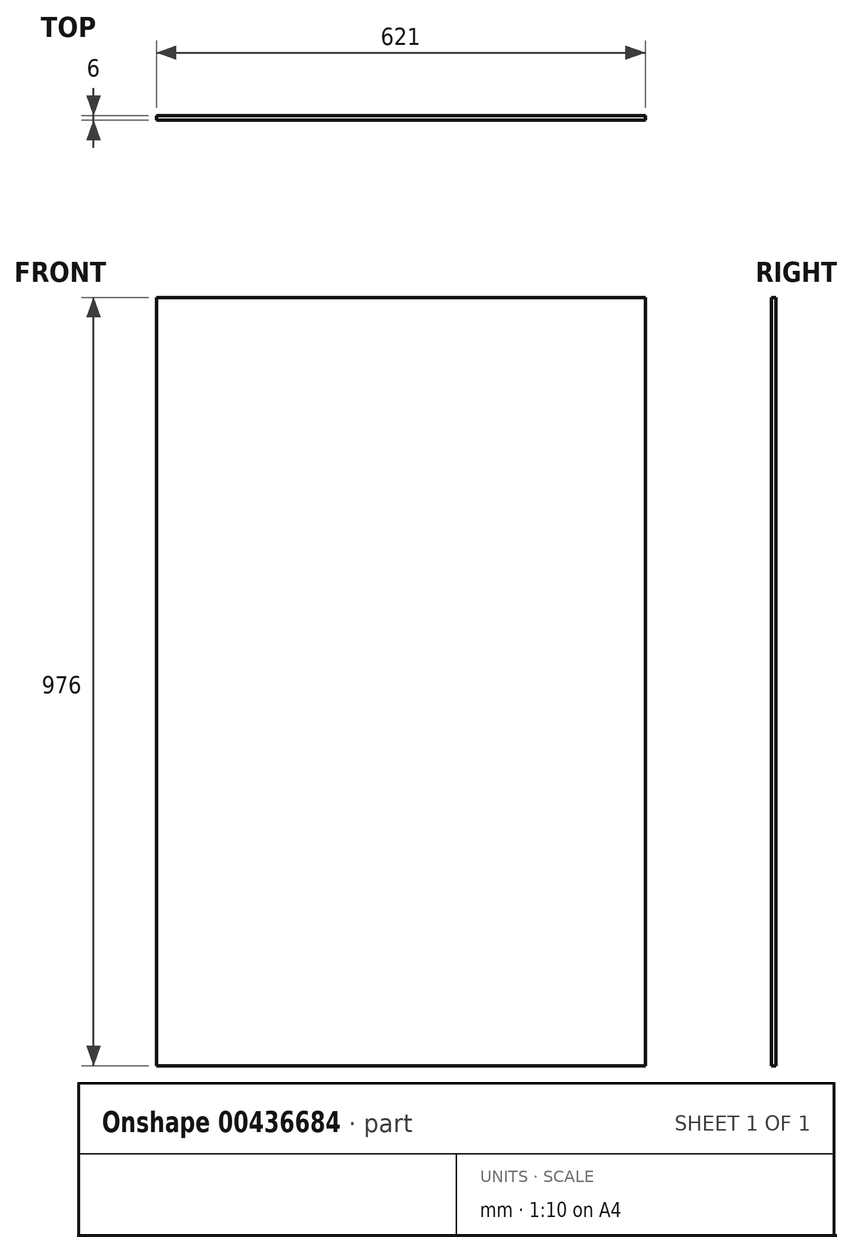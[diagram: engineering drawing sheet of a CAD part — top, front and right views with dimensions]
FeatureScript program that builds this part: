
annotation { "Feature Type Name" : "Feature", "Feature Type Description" : "" }
export const myFeature = defineFeature(function(context is Context, id is Id, definition is map)
    precondition{}
    {
        {
            var Q0;
            Q0=qCreatedBy(makeId("Front.planeOp"),FACE);
            var sketch = newSketch(context, id + "F0", { "sketchPlane" : qUnion([Q0])});
            skLineSegment(sketch, "E0.bottom", {"start": v(310.5, 488) * mm, "end": v(-310.5, 488) * mm});
            skLineSegment(sketch, "E0.top", {"start": v(310.5, -488) * mm, "end": v(-310.5, -488) * mm});
            skLineSegment(sketch, "E0.left", {"start": v(310.5, 488) * mm, "end": v(310.5, -488) * mm});
            skLineSegment(sketch, "E0.right", {"start": v(-310.5, 488) * mm, "end": v(-310.5, -488) * mm});
            skPoint(sketch, "E0.middle", {"position": v(0, 0) * mm});
            skSolve(sketch);
        }
        {
            var Q0;
            Q0=qSketchRegion(id+"F0",true);
            extrude(context, id + "F1", {"entities" : qUnion([Q0]), "depth" : 6 * mm});
        }
    });
